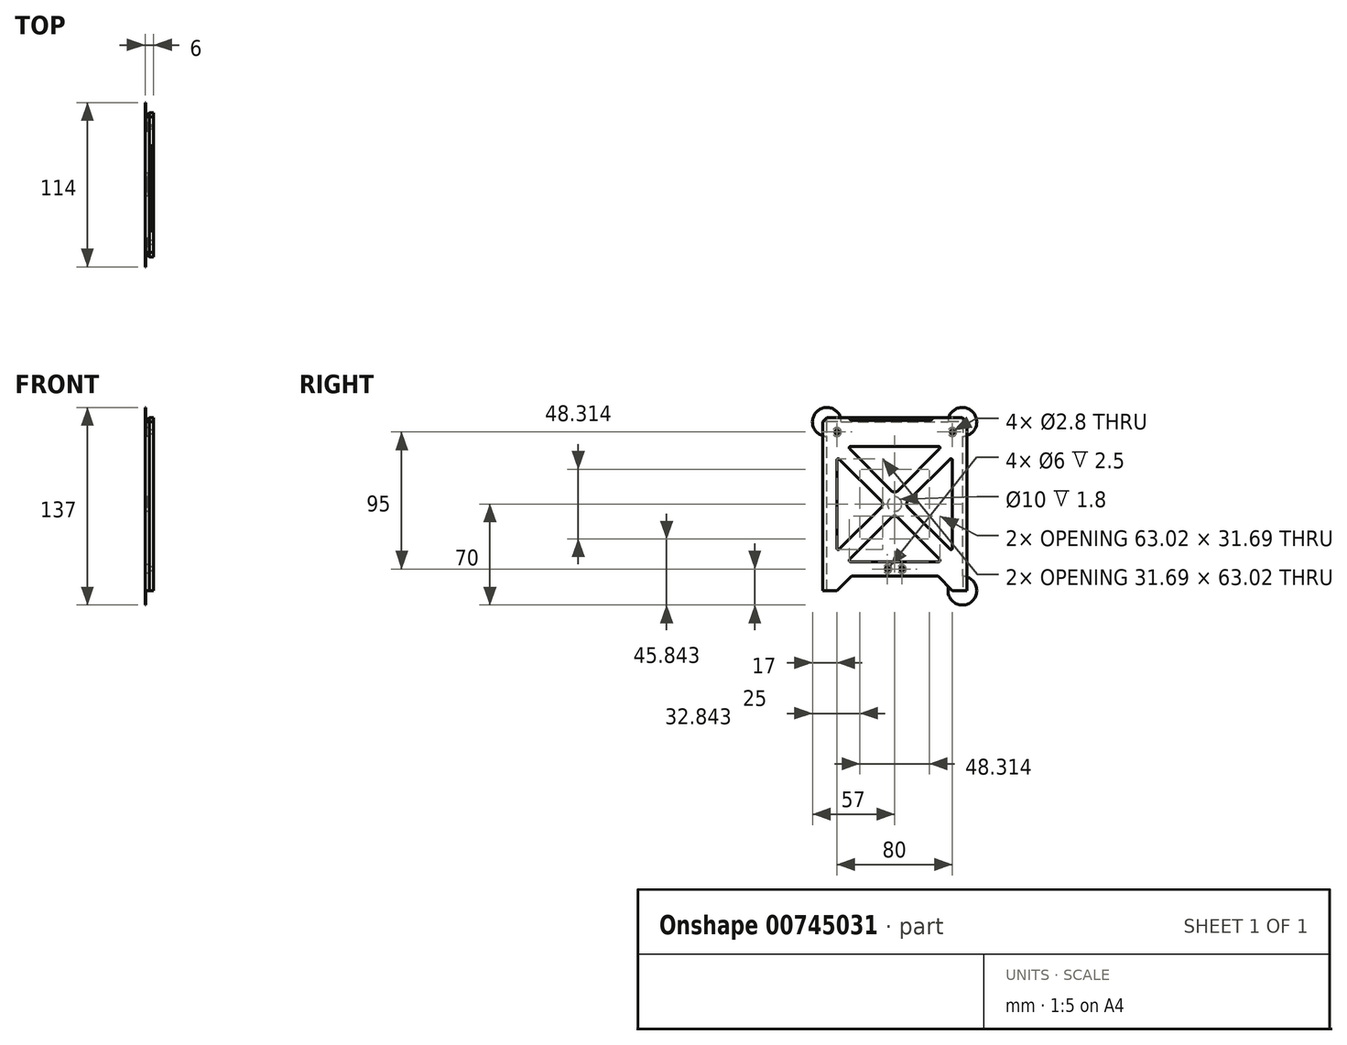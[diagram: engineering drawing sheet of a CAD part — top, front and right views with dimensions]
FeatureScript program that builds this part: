
annotation { "Feature Type Name" : "Feature", "Feature Type Description" : "" }
export const myFeature = defineFeature(function(context is Context, id is Id, definition is map)
    precondition{}
    {
        {
            var Q0;
            Q0=qCreatedBy(makeId("Right.planeOp"),FACE);
            var sketch = newSketch(context, id + "F0", { "sketchPlane" : qUnion([Q0])});
            skLineSegment(sketch, "E0.bottom", {"start": v(50, -60) * mm, "end": v(40.05, -60) * mm});
            skLineSegment(sketch, "E0.top", {"start": v(50, 60) * mm, "end": v(-50, 60) * mm});
            skLineSegment(sketch, "E0.left", {"start": v(50, -60) * mm, "end": v(50, 60) * mm});
            skLineSegment(sketch, "E0.right", {"start": v(-50, -60) * mm, "end": v(-50, 60) * mm});
            skPoint(sketch, "E0.middle", {"position": v(0, 0) * mm});
            skLineSegment(sketch, "E1.bottom", {"start": v(40, -40) * mm, "end": v(-32.93, -40) * mm});
            skLineSegment(sketch, "E1.top", {"start": v(32.93, 40) * mm, "end": v(-32.93, 40) * mm});
            skLineSegment(sketch, "E1.left", {"start": v(40, -40) * mm, "end": v(40, 32.93) * mm});
            skLineSegment(sketch, "E1.right", {"start": v(-40, -32.93) * mm, "end": v(-40, 32.93) * mm});
            skLineSegment(sketch, "E2.trimOffspring", {"start": v(-40, -60) * mm, "end": v(-50, -60) * mm});
            skLineSegment(sketch, "E3", {"start": v(30.05, -50) * mm, "end": v(40.05, -60) * mm});
            skLineSegment(sketch, "E4", {"start": v(30.05, -50) * mm, "end": v(-29.95, -50) * mm});
            skLineSegment(sketch, "E5", {"start": v(-29.95, -50) * mm, "end": v(-40, -60) * mm});
            skLineSegment(sketch, "E6", {"start": v(-40, -32.93) * mm, "end": v(-9.2, -2.12) * mm});
            skLineSegment(sketch, "E7.MirrorCS", {"start": v(-32.93, -40) * mm, "end": v(-2.12, -9.2) * mm});
            skLineSegment(sketch, "E8.trimOffspring", {"start": v(-40, 32.93) * mm, "end": v(-9.2, 2.12) * mm});
            skLineSegment(sketch, "E9.MirrorCS", {"start": v(-32.93, 40) * mm, "end": v(-2.12, 9.2) * mm});
            skLineSegment(sketch, "E10.trimOffspring", {"start": v(9.2, 2.12) * mm, "end": v(40, 32.93) * mm});
            skLineSegment(sketch, "E11.trimOffspring", {"start": v(2.12, -9.2) * mm, "end": v(32.93, -40) * mm});
            skLineSegment(sketch, "E12.trimOffspring", {"start": v(9.2, -2.12) * mm, "end": v(40, -32.93) * mm});
            skLineSegment(sketch, "E13.trimOffspring", {"start": v(2.12, 9.2) * mm, "end": v(32.93, 40) * mm});
            skPoint(sketch, "E14.visualSharp", {"position": v(0, 7.07) * mm});
            skArc(sketch, "E14.filletArc", {"start": v(-2.12, 9.2) * mm, "mid": v(0, 8.31) * mm, "end": v(2.12, 9.2) * mm});
            skPoint(sketch, "E15.visualSharp", {"position": v(0, -7.07) * mm});
            skArc(sketch, "E15.filletArc", {"start": v(2.12, -9.2) * mm, "mid": v(0, -8.31) * mm, "end": v(-2.12, -9.2) * mm});
            skPoint(sketch, "E16.visualSharp", {"position": v(7.07, 0) * mm});
            skArc(sketch, "E16.filletArc", {"start": v(9.2, 2.12) * mm, "mid": v(8.31, 0) * mm, "end": v(9.2, -2.12) * mm});
            skPoint(sketch, "E17.visualSharp", {"position": v(-7.07, 0) * mm});
            skArc(sketch, "E17.filletArc", {"start": v(-9.2, -2.12) * mm, "mid": v(-8.31, 0) * mm, "end": v(-9.2, 2.12) * mm});
            skLineSegment(sketch, "E18", {"start": v(81.83, 50) * mm, "end": v(-92.03, 50) * mm, "construction": true});
            skPoint(sketch, "E19", {"position": v(40, 50) * mm});
            skPoint(sketch, "E20", {"position": v(-40, 50) * mm});
            skSolve(sketch);
        }
        {
            var Q0;
            Q0=qSketchRegion(id+"F0",true);
            extrude(context, id + "F1", {"entities" : qUnion([Q0]), "depth" : 6 * mm, "offsetDistance" : 25 * mm});
        }
        {
            var Q0;
            Q0=makeQuery(id+"F1.opExtrude","SWEPT_EDGE",EDGE,{"disambiguationData":[OSD([sQuery(id+"F0.wireOp",EDGE,"E1.top"),sQuery(id+"F0.wireOp",EDGE,"E9.MirrorCS")])]});
            var Q1;
            Q1=makeQuery(id+"F1.opExtrude","SWEPT_EDGE",EDGE,{"disambiguationData":[OSD([sQuery(id+"F0.wireOp",EDGE,"E1.top"),sQuery(id+"F0.wireOp",EDGE,"E13.trimOffspring")])]});
            var Q2;
            Q2=makeQuery(id+"F1.opExtrude","SWEPT_EDGE",EDGE,{"disambiguationData":[OSD([sQuery(id+"F0.wireOp",EDGE,"E1.right"),sQuery(id+"F0.wireOp",EDGE,"E8.trimOffspring")])]});
            var Q3;
            Q3=makeQuery(id+"F1.opExtrude","SWEPT_EDGE",EDGE,{"disambiguationData":[OSD([sQuery(id+"F0.wireOp",EDGE,"E1.right"),sQuery(id+"F0.wireOp",EDGE,"E6")])]});
            var Q4;
            Q4=makeQuery(id+"F1.opExtrude","SWEPT_EDGE",EDGE,{"disambiguationData":[OSD([sQuery(id+"F0.wireOp",EDGE,"E1.bottom"),sQuery(id+"F0.wireOp",EDGE,"E7.MirrorCS")])]});
            var Q5;
            Q5=makeQuery(id+"F1.opExtrude","SWEPT_EDGE",EDGE,{"disambiguationData":[OSD([sQuery(id+"F0.wireOp",EDGE,"E1.left"),sQuery(id+"F0.wireOp",EDGE,"E10.trimOffspring")])]});
            var Q6;
            Q6=makeQuery(id+"F1.opExtrude","SWEPT_EDGE",EDGE,{"disambiguationData":[OSD([sQuery(id+"F0.wireOp",EDGE,"E1.left"),sQuery(id+"F0.wireOp",EDGE,"E12.trimOffspring")])]});
            var Q7;
            Q7=makeQuery(id+"F1.opExtrude","SWEPT_EDGE",EDGE,{"disambiguationData":[OSD([sQuery(id+"F0.wireOp",EDGE,"E1.bottom"),sQuery(id+"F0.wireOp",EDGE,"E11.trimOffspring")])]});
            fillet(context, id + "F2", {"entities" : qUnion([Q0, Q1, Q2, Q3, Q4, Q5, Q6, Q7]), "radius" : 1 * mm, "tangentPropagation" : true, "allowEdgeOverflow" : false});
        }
        {
            var Q0;
            Q0=sQuery(id+"F0.wireOp",VERTEX,"E20");
            var Q1;
            Q1=sQuery(id+"F0.wireOp",VERTEX,"E19");
            var Q2;
            Q2=makeQuery(id+"F1.opExtrude","SWEPT_BODY",BODY,{"disambiguationData":[OSD([sQuery(id+"F0.wireOp",EDGE,"E0.bottom"),sQuery(id+"F0.wireOp",EDGE,"E0.top"),sQuery(id+"F0.wireOp",EDGE,"E0.left"),sQuery(id+"F0.wireOp",EDGE,"E0.right"),sQuery(id+"F0.wireOp",EDGE,"E1.bottom"),sQuery(id+"F0.wireOp",EDGE,"E1.top"),sQuery(id+"F0.wireOp",EDGE,"E1.left"),sQuery(id+"F0.wireOp",EDGE,"E1.right"),sQuery(id+"F0.wireOp",EDGE,"E2.trimOffspring"),sQuery(id+"F0.wireOp",EDGE,"E3"),sQuery(id+"F0.wireOp",EDGE,"E4"),sQuery(id+"F0.wireOp",EDGE,"E5"),sQuery(id+"F0.wireOp",EDGE,"E6"),sQuery(id+"F0.wireOp",EDGE,"E7.MirrorCS"),sQuery(id+"F0.wireOp",EDGE,"E8.trimOffspring"),sQuery(id+"F0.wireOp",EDGE,"E9.MirrorCS"),sQuery(id+"F0.wireOp",EDGE,"E10.trimOffspring"),sQuery(id+"F0.wireOp",EDGE,"E11.trimOffspring"),sQuery(id+"F0.wireOp",EDGE,"E12.trimOffspring"),sQuery(id+"F0.wireOp",EDGE,"E13.trimOffspring"),sQuery(id+"F0.wireOp",EDGE,"E14.filletArc"),sQuery(id+"F0.wireOp",EDGE,"E15.filletArc"),sQuery(id+"F0.wireOp",EDGE,"E16.filletArc"),sQuery(id+"F0.wireOp",EDGE,"E17.filletArc")])]});
            hole(context, id + "F3", {"style" : HoleStyle.C_BORE, "endStyle" : HoleEndStyle.THROUGH, "oppositeDirection" : true, "holeDiameter" : 2.8 * mm, "cBoreDiameter" : 6 * mm, "cBoreDepth" : 2.5 * mm, "majorDiameter" : 5 * mm, "isTappedThrough" : true, "tappedDepth" : 6 * mm, "tapClearance" : 3, "locations" : qUnion([Q0, Q1]), "scope" : qUnion([Q2])});
        }
        {
            var Q0;
            Q0=makeQuery(id+"F1.opExtrude","CAP_FACE",FACE,{"disambiguationData":[OSD([sQuery(id+"F0.wireOp",EDGE,"E0.bottom"),sQuery(id+"F0.wireOp",EDGE,"E0.top"),sQuery(id+"F0.wireOp",EDGE,"E0.left"),sQuery(id+"F0.wireOp",EDGE,"E0.right"),sQuery(id+"F0.wireOp",EDGE,"E1.bottom"),sQuery(id+"F0.wireOp",EDGE,"E1.top"),sQuery(id+"F0.wireOp",EDGE,"E1.left"),sQuery(id+"F0.wireOp",EDGE,"E1.right"),sQuery(id+"F0.wireOp",EDGE,"E2.trimOffspring"),sQuery(id+"F0.wireOp",EDGE,"E3"),sQuery(id+"F0.wireOp",EDGE,"E4"),sQuery(id+"F0.wireOp",EDGE,"E5"),sQuery(id+"F0.wireOp",EDGE,"E6"),sQuery(id+"F0.wireOp",EDGE,"E7.MirrorCS"),sQuery(id+"F0.wireOp",EDGE,"E8.trimOffspring"),sQuery(id+"F0.wireOp",EDGE,"E9.MirrorCS"),sQuery(id+"F0.wireOp",EDGE,"E10.trimOffspring"),sQuery(id+"F0.wireOp",EDGE,"E11.trimOffspring"),sQuery(id+"F0.wireOp",EDGE,"E12.trimOffspring"),sQuery(id+"F0.wireOp",EDGE,"E13.trimOffspring"),sQuery(id+"F0.wireOp",EDGE,"E14.filletArc"),sQuery(id+"F0.wireOp",EDGE,"E15.filletArc"),sQuery(id+"F0.wireOp",EDGE,"E16.filletArc"),sQuery(id+"F0.wireOp",EDGE,"E17.filletArc")])],"isStart":true});
            var sketch = newSketch(context, id + "F4", { "sketchPlane" : qUnion([Q0])});
            skCircle(sketch, "E21", {"center": v(0, 0) * mm, "radius": 5 * mm});
            skSolve(sketch);
        }
        {
            var Q0;
            Q0=makeQuery(id+"F4.imprint","IMPRINT",FACE,{"disambiguationData":[TD([[makeQuery(id+"F4.imprint","IMPRINT",EDGE,{"derivedFrom":sQuery(id+"F4.wireOp",EDGE,"E21")}),1.0]])]});
            extrude(context, id + "F5", {"entities" : qUnion([Q0]), "operationType" : NewBodyOperationType.REMOVE, "oppositeDirection" : true, "depth" : 1.8 * mm, "offsetDistance" : 25 * mm});
        }
        {
            var Q0;
            {var subQ0=sQuery(id+"F0.wireOp",EDGE,"E0.left");var subQ1=sQuery(id+"F0.wireOp",EDGE,"E0.top");var subQ2=sQuery(id+"F0.wireOp",EDGE,"E0.right");var subQ3=sQuery(id+"F0.wireOp",EDGE,"E2.trimOffspring");var subQ4=sQuery(id+"F0.wireOp",EDGE,"E0.bottom");Q0=makeQuery(id+"F10.boolean.opBoolean","MERGE",FACE,{"derivedFrom":[makeQuery(id+"F1.opExtrude","CAP_FACE",FACE,{"disambiguationData":[OSD([subQ4,subQ1,subQ0,subQ2,sQuery(id+"F0.wireOp",EDGE,"E1.bottom"),sQuery(id+"F0.wireOp",EDGE,"E1.top"),sQuery(id+"F0.wireOp",EDGE,"E1.left"),sQuery(id+"F0.wireOp",EDGE,"E1.right"),subQ3,sQuery(id+"F0.wireOp",EDGE,"E3"),sQuery(id+"F0.wireOp",EDGE,"E4"),sQuery(id+"F0.wireOp",EDGE,"E5"),sQuery(id+"F0.wireOp",EDGE,"E6"),sQuery(id+"F0.wireOp",EDGE,"E7.MirrorCS"),sQuery(id+"F0.wireOp",EDGE,"E8.trimOffspring"),sQuery(id+"F0.wireOp",EDGE,"E9.MirrorCS"),sQuery(id+"F0.wireOp",EDGE,"E10.trimOffspring"),sQuery(id+"F0.wireOp",EDGE,"E11.trimOffspring"),sQuery(id+"F0.wireOp",EDGE,"E12.trimOffspring"),sQuery(id+"F0.wireOp",EDGE,"E13.trimOffspring"),sQuery(id+"F0.wireOp",EDGE,"E14.filletArc"),sQuery(id+"F0.wireOp",EDGE,"E15.filletArc"),sQuery(id+"F0.wireOp",EDGE,"E16.filletArc"),sQuery(id+"F0.wireOp",EDGE,"E17.filletArc")])],"isStart":true}),makeQuery(id+"F10.opExtrude","CAP_FACE",FACE,{"disambiguationData":[OSD([subQ4,subQ0,sQuery(id+"F9.wireOp",EDGE,"PSrgGkol-MO8q-g1fu-dDRE-y41ujJaxh7FT")])],"isStart":true}),makeQuery(id+"F10.opExtrude","CAP_FACE",FACE,{"disambiguationData":[OSD([subQ2,subQ3,sQuery(id+"F9.wireOp",EDGE,"1aKPLW1Y-IE5d-4tmK-5bFR-xkpx61fHem11")])],"isStart":true}),makeQuery(id+"F10.opExtrude","CAP_FACE",FACE,{"disambiguationData":[OSD([subQ1,subQ2,sQuery(id+"F9.wireOp",EDGE,"02GekRd3-WHB3-A6C6-mmOw-hFaiTY61e2sP")])],"isStart":true}),makeQuery(id+"F10.opExtrude","CAP_FACE",FACE,{"disambiguationData":[OSD([subQ1,subQ0,sQuery(id+"F9.wireOp",EDGE,"ECdukxah-RqsZ-JlNO-yzCW-vx4sxx8bxQE0")])],"isStart":true})]});}
            var sketch = newSketch(context, id + "F6", { "sketchPlane" : qUnion([Q0])});
            skPoint(sketch, "E22", {"position": v(-5, -45) * mm});
            skPoint(sketch, "E23.MirrorP", {"position": v(5, -45) * mm});
            skSolve(sketch);
        }
        {
            var Q0;
            Q0=sQuery(id+"F6.wireOp",VERTEX,"E22");
            var Q1;
            Q1=sQuery(id+"F6.wireOp",VERTEX,"E23.MirrorP");
            var Q2;
            Q2=makeQuery(id+"F1.opExtrude","SWEPT_BODY",BODY,{"disambiguationData":[OSD([sQuery(id+"F0.wireOp",EDGE,"E0.bottom"),sQuery(id+"F0.wireOp",EDGE,"E0.top"),sQuery(id+"F0.wireOp",EDGE,"E0.left"),sQuery(id+"F0.wireOp",EDGE,"E0.right"),sQuery(id+"F0.wireOp",EDGE,"E1.bottom"),sQuery(id+"F0.wireOp",EDGE,"E1.top"),sQuery(id+"F0.wireOp",EDGE,"E1.left"),sQuery(id+"F0.wireOp",EDGE,"E1.right"),sQuery(id+"F0.wireOp",EDGE,"E2.trimOffspring"),sQuery(id+"F0.wireOp",EDGE,"E3"),sQuery(id+"F0.wireOp",EDGE,"E4"),sQuery(id+"F0.wireOp",EDGE,"E5"),sQuery(id+"F0.wireOp",EDGE,"E6"),sQuery(id+"F0.wireOp",EDGE,"E7.MirrorCS"),sQuery(id+"F0.wireOp",EDGE,"E8.trimOffspring"),sQuery(id+"F0.wireOp",EDGE,"E9.MirrorCS"),sQuery(id+"F0.wireOp",EDGE,"E10.trimOffspring"),sQuery(id+"F0.wireOp",EDGE,"E11.trimOffspring"),sQuery(id+"F0.wireOp",EDGE,"E12.trimOffspring"),sQuery(id+"F0.wireOp",EDGE,"E13.trimOffspring"),sQuery(id+"F0.wireOp",EDGE,"E14.filletArc"),sQuery(id+"F0.wireOp",EDGE,"E15.filletArc"),sQuery(id+"F0.wireOp",EDGE,"E16.filletArc"),sQuery(id+"F0.wireOp",EDGE,"E17.filletArc")])]});
            hole(context, id + "F7", {"style" : HoleStyle.C_BORE, "endStyle" : HoleEndStyle.THROUGH, "holeDiameter" : 2.8 * mm, "cBoreDiameter" : 6 * mm, "cBoreDepth" : 2.5 * mm, "majorDiameter" : 5 * mm, "isTappedThrough" : true, "tappedDepth" : 6 * mm, "tapClearance" : 3, "locations" : qUnion([Q0, Q1]), "scope" : qUnion([Q2])});
        }
        {
            var Q0;
            Q0=makeQuery(id+"F1.opExtrude","SWEPT_EDGE",EDGE,{"disambiguationData":[OSD([sQuery(id+"F0.wireOp",EDGE,"E0.top"),sQuery(id+"F0.wireOp",EDGE,"E0.right")])]});
            var Q1;
            Q1=makeQuery(id+"F1.opExtrude","SWEPT_EDGE",EDGE,{"disambiguationData":[OSD([sQuery(id+"F0.wireOp",EDGE,"E0.top"),sQuery(id+"F0.wireOp",EDGE,"E0.left")])]});
            var Q2;
            Q2=makeQuery(id+"F1.opExtrude","CAP_EDGE",EDGE,{"disambiguationData":[OSD([sQuery(id+"F0.wireOp",EDGE,"E0.right")])],"isStart":true});
            var Q3;
            Q3=makeQuery(id+"F1.opExtrude","CAP_EDGE",EDGE,{"disambiguationData":[OSD([sQuery(id+"F0.wireOp",EDGE,"E0.left")])],"isStart":true});
            var Q4;
            Q4=makeQuery(id+"F1.opExtrude","CAP_EDGE",EDGE,{"disambiguationData":[OSD([sQuery(id+"F0.wireOp",EDGE,"E0.top")])],"isStart":true});
            chamfer(context, id + "F8", {"entities" : qUnion([Q0, Q1, Q2, Q3, Q4]), "width" : 3 * mm, "tangentPropagation" : true});
        }
        {
            var Q0;
            Q0=makeQuery(id+"F1.opExtrude","CAP_FACE",FACE,{"disambiguationData":[OSD([sQuery(id+"F0.wireOp",EDGE,"E0.bottom"),sQuery(id+"F0.wireOp",EDGE,"E0.top"),sQuery(id+"F0.wireOp",EDGE,"E0.left"),sQuery(id+"F0.wireOp",EDGE,"E0.right"),sQuery(id+"F0.wireOp",EDGE,"E1.bottom"),sQuery(id+"F0.wireOp",EDGE,"E1.top"),sQuery(id+"F0.wireOp",EDGE,"E1.left"),sQuery(id+"F0.wireOp",EDGE,"E1.right"),sQuery(id+"F0.wireOp",EDGE,"E2.trimOffspring"),sQuery(id+"F0.wireOp",EDGE,"E3"),sQuery(id+"F0.wireOp",EDGE,"E4"),sQuery(id+"F0.wireOp",EDGE,"E5"),sQuery(id+"F0.wireOp",EDGE,"E6"),sQuery(id+"F0.wireOp",EDGE,"E7.MirrorCS"),sQuery(id+"F0.wireOp",EDGE,"E8.trimOffspring"),sQuery(id+"F0.wireOp",EDGE,"E9.MirrorCS"),sQuery(id+"F0.wireOp",EDGE,"E10.trimOffspring"),sQuery(id+"F0.wireOp",EDGE,"E11.trimOffspring"),sQuery(id+"F0.wireOp",EDGE,"E12.trimOffspring"),sQuery(id+"F0.wireOp",EDGE,"E13.trimOffspring"),sQuery(id+"F0.wireOp",EDGE,"E14.filletArc"),sQuery(id+"F0.wireOp",EDGE,"E15.filletArc"),sQuery(id+"F0.wireOp",EDGE,"E16.filletArc"),sQuery(id+"F0.wireOp",EDGE,"E17.filletArc")])],"isStart":true});
            var sketch = newSketch(context, id + "F9", { "sketchPlane" : qUnion([Q0])});
            skPoint(sketch, "E24", {"position": v(-47, 57) * mm});
            skPoint(sketch, "E25", {"position": v(47, 57) * mm});
            skPoint(sketch, "E26", {"position": v(47, -60) * mm});
            skPoint(sketch, "E27", {"position": v(-47, -60) * mm});
            skArc(sketch, "E28", {"start": v(-37, 57) * mm, "mid": v(-54.07, 64.07) * mm, "end": v(-47, 47) * mm});
            skArc(sketch, "E29", {"start": v(47, 47) * mm, "mid": v(54.07, 64.07) * mm, "end": v(37, 57) * mm});
            skArc(sketch, "E30", {"start": v(47, -50) * mm, "mid": v(53.07, -67.95) * mm, "end": v(37.35, -57.37) * mm});
            skArc(sketch, "E31", {"start": v(-47, -50) * mm, "mid": v(-53.05, -67.96) * mm, "end": v(-37.37, -57.32) * mm});
            skSolve(sketch);
        }
        {
            var Q0;
            {var subQ0=sQuery(id+"F9.wireOp",EDGE,"E28");Q0=makeQuery(id+"F9.imprint","IMPRINT",FACE,{"disambiguationData":[TD([[makeQuery(id+"F9.imprint","IMPRINT",EDGE,{"derivedFrom":subQ0}),1.0]])]});}
            var Q1;
            {var subQ0=sQuery(id+"F9.wireOp",EDGE,"E29");Q1=makeQuery(id+"F9.imprint","IMPRINT",FACE,{"disambiguationData":[TD([[makeQuery(id+"F9.imprint","IMPRINT",EDGE,{"derivedFrom":subQ0}),1.0]])]});}
            var Q2;
            {var subQ0=sQuery(id+"F9.wireOp",EDGE,"E31");Q2=makeQuery(id+"F9.imprint","IMPRINT",FACE,{"disambiguationData":[TD([[makeQuery(id+"F9.imprint","IMPRINT",EDGE,{"derivedFrom":subQ0}),1.0]])]});}
            var Q3;
            {var subQ0=sQuery(id+"F9.wireOp",EDGE,"E30");Q3=makeQuery(id+"F9.imprint","IMPRINT",FACE,{"disambiguationData":[TD([[makeQuery(id+"F9.imprint","IMPRINT",EDGE,{"derivedFrom":subQ0}),-1.0]])]});}
            extrude(context, id + "F10", {"entities" : qUnion([Q0, Q1, Q2, Q3]), "operationType" : NewBodyOperationType.ADD, "oppositeDirection" : true, "depth" : 0.4 * mm, "offsetDistance" : 25 * mm});
        }
        {
            var Q0;
            Q0=makeQuery(id+"F1.opExtrude","SWEPT_FACE",FACE,{"disambiguationData":[OSD([sQuery(id+"F0.wireOp",EDGE,"E0.top")])]});
            var sketch = newSketch(context, id + "F11", { "sketchPlane" : qUnion([Q0])});
            skLineSegment(sketch, "E32.bottom", {"start": v(6, -32) * mm, "end": v(4, -32) * mm});
            skLineSegment(sketch, "E32.top", {"start": v(6, 27) * mm, "end": v(4, 27) * mm});
            skLineSegment(sketch, "E32.left", {"start": v(6, -32) * mm, "end": v(6, 27) * mm});
            skLineSegment(sketch, "E32.right", {"start": v(4, -32) * mm, "end": v(4, 27) * mm});
            skSolve(sketch);
        }
        {
            var Q0;
            Q0=makeQuery(id+"F11.imprint","IMPRINT",FACE,{"disambiguationData":[TD([[makeQuery(id+"F11.imprint","IMPRINT",EDGE,{"derivedFrom":sQuery(id+"F11.wireOp",EDGE,"E32.bottom")}),-1.0]])]});
            extrude(context, id + "F12", {"entities" : qUnion([Q0]), "operationType" : NewBodyOperationType.REMOVE, "oppositeDirection" : true, "depth" : 2 * mm, "offsetDistance" : 25 * mm});
        }
        {
            var Q0;
            Q0=makeQuery(id+"F12.boolean.opBoolean","COPY",EDGE,{"derivedFrom":makeQuery(id+"F12.opExtrude","CAP_EDGE",EDGE,{"disambiguationData":[OSD([sQuery(id+"F11.wireOp",EDGE,"E32.right")])],"isStart":false})});
            var Q1;
            Q1=makeQuery(id+"F12.boolean.opBoolean","COPY",EDGE,{"derivedFrom":makeQuery(id+"F12.opExtrude","CAP_EDGE",EDGE,{"disambiguationData":[OSD([sQuery(id+"F11.wireOp",EDGE,"E32.top")])],"isStart":false})});
            var Q2;
            Q2=makeQuery(id+"F12.boolean.opBoolean","COPY",EDGE,{"derivedFrom":makeQuery(id+"F12.opExtrude","CAP_EDGE",EDGE,{"disambiguationData":[OSD([sQuery(id+"F11.wireOp",EDGE,"E32.bottom")])],"isStart":false})});
            chamfer(context, id + "F13", {"entities" : qUnion([Q0, Q1, Q2]), "width" : 2 * mm, "tangentPropagation" : true});
        }
    });
